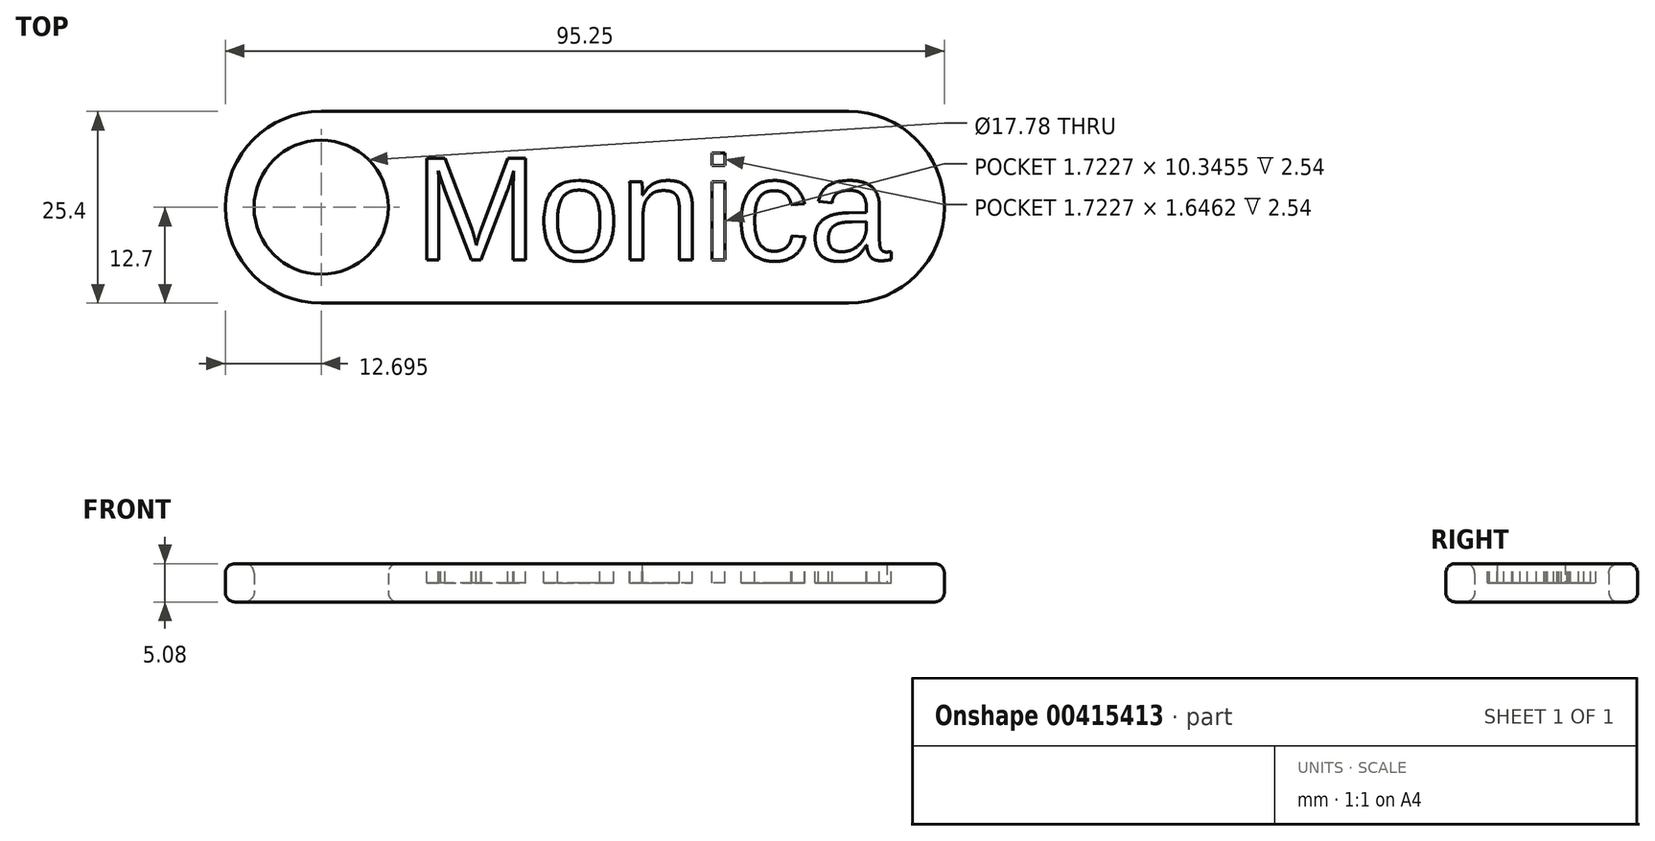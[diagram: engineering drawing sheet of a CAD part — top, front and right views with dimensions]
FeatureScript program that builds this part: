
annotation { "Feature Type Name" : "Feature", "Feature Type Description" : "" }
export const myFeature = defineFeature(function(context is Context, id is Id, definition is map)
    precondition{}
    {
        {
            var Q0;
            Q0=qCreatedBy(makeId("Top.planeOp"),FACE);
            var sketch = newSketch(context, id + "F0", { "sketchPlane" : qUnion([Q0])});
            skLineSegment(sketch, "E0.bottom", {"start": v(34.93, -12.7) * mm, "end": v(-34.93, -12.7) * mm});
            skLineSegment(sketch, "E0.top", {"start": v(34.93, 12.7) * mm, "end": v(-34.93, 12.7) * mm});
            skPoint(sketch, "E0.middle", {"position": v(0, 0) * mm});
            skArc(sketch, "E1", {"start": v(34.93, -12.7) * mm, "mid": v(47.63, 0) * mm, "end": v(34.93, 12.7) * mm});
            skArc(sketch, "E2", {"start": v(-34.93, 12.7) * mm, "mid": v(-47.63, 0) * mm, "end": v(-34.93, -12.7) * mm});
            skCircle(sketch, "E3", {"center": v(-34.93, 0) * mm, "radius": 8.9 * mm});
            skSolve(sketch);
        }
        {
            var Q0;
            Q0=makeQuery(id+"F0.imprint","IMPRINT",FACE,{"disambiguationData":[TD([[makeQuery(id+"F0.imprint","IMPRINT",EDGE,{"derivedFrom":sQuery(id+"F0.wireOp",EDGE,"E0.bottom")}),-1.0]])]});
            extrude(context, id + "F1", {"entities" : qUnion([Q0]), "depth" : 5.08 * mm});
        }
        {
            var Q0;
            Q0=makeQuery(id+"F1.opExtrude","CAP_FACE",FACE,{"disambiguationData":[OSD([sQuery(id+"F0.wireOp",EDGE,"E0.bottom"),sQuery(id+"F0.wireOp",EDGE,"E0.top"),sQuery(id+"F0.wireOp",EDGE,"E1"),sQuery(id+"F0.wireOp",EDGE,"E2"),sQuery(id+"F0.wireOp",EDGE,"E3")])],"isStart":false});
            var sketch = newSketch(context, id + "F2", { "sketchPlane" : qUnion([Q0])});
            skText(sketch, "E4", { "text": " Monica", "fontName": "Arimo-Regular.ttf"});
            const initialGuessF2  = {"E4": [-0.028, -0.00699, 1, 0, 0.0141]};
            skSetInitialGuess(sketch, initialGuessF2);
            skSolve(sketch);
        }
        {
            var Q0;
            Q0=qSketchRegion(id+"F2",true);
            extrude(context, id + "F3", {"entities" : qUnion([Q0]), "operationType" : NewBodyOperationType.REMOVE, "oppositeDirection" : true, "depth" : 2.54 * mm});
        }
        {
            var Q0;
            Q0=makeQuery(id+"F1.opExtrude","CAP_EDGE",EDGE,{"disambiguationData":[OSD([sQuery(id+"F0.wireOp",EDGE,"E2")])],"isStart":false});
            var Q1;
            Q1=makeQuery(id+"F1.opExtrude","CAP_FACE",FACE,{"disambiguationData":[OSD([sQuery(id+"F0.wireOp",EDGE,"E0.bottom"),sQuery(id+"F0.wireOp",EDGE,"E0.top"),sQuery(id+"F0.wireOp",EDGE,"E1"),sQuery(id+"F0.wireOp",EDGE,"E2"),sQuery(id+"F0.wireOp",EDGE,"E3")])],"isStart":true});
            var Q2;
            Q2=makeQuery(id+"F1.opExtrude","CAP_EDGE",EDGE,{"disambiguationData":[OSD([sQuery(id+"F0.wireOp",EDGE,"E3")])],"isStart":false});
            fillet(context, id + "F4", {"entities" : qUnion([Q0, Q1, Q2]), "radius" : 1.27 * mm, "tangentPropagation" : true, "allowEdgeOverflow" : false});
        }
    });
